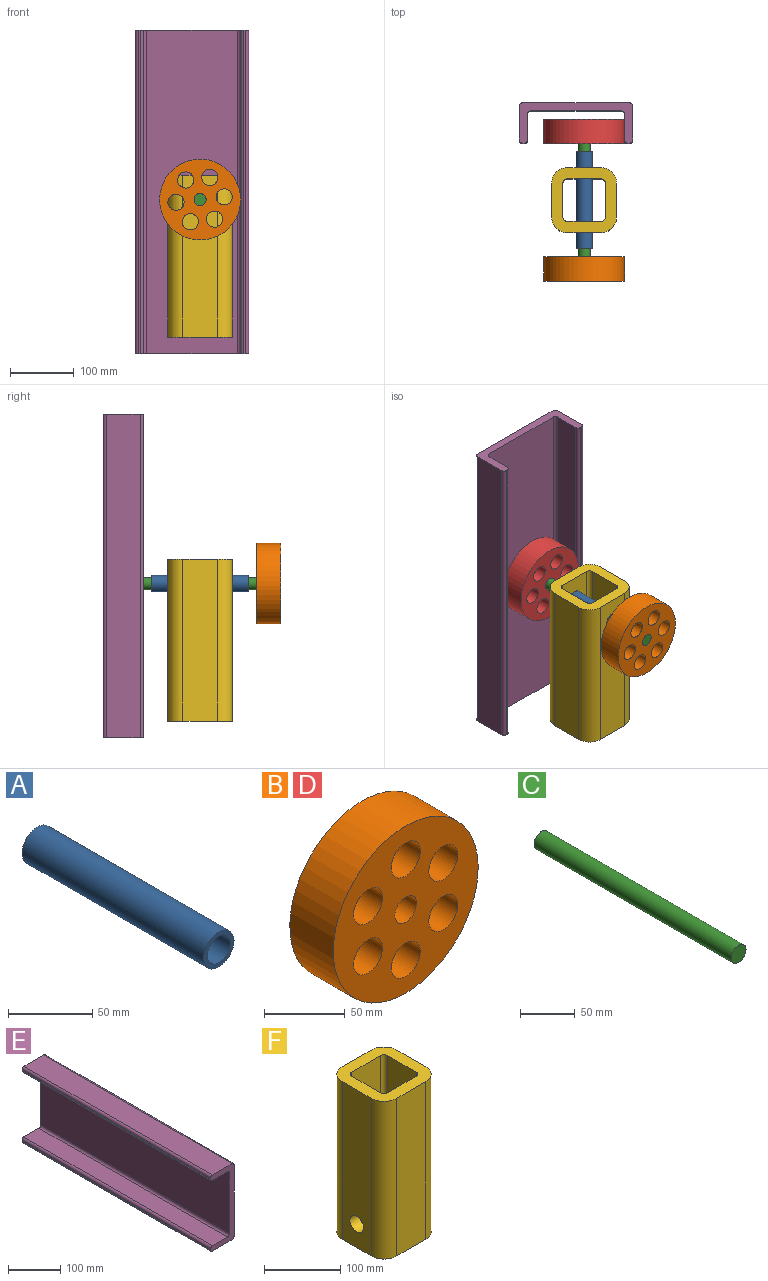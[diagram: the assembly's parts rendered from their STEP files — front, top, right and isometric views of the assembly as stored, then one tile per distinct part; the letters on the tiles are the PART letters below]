
ASSEMBLY  parts=6 mates=5
PART A: 4 faces, bbox 25.4x152.4x25.4 mm
  f0: cylinder r=9.53mm len=152.4mm, axis (0,1,0), area 9120.7mm2, adj f2,f3
  f1: cylinder r=12.7mm len=152.4mm, axis (0,1,0), area 12161mm2, adj f2,f3
  f2: plane 25.4x25.4mm, normal (0,-1,0), area 221.7mm2, adj f0,f1
  f3: plane 25.4x25.4mm, normal (0,1,0), area 221.7mm2, adj f0,f1
PART B: 10 faces, bbox 127x38.1x127 mm
  f0: cylinder r=9.53mm len=38.1mm, axis (0,1,0), area 2280.2mm2, adj f2,f3
  f1: cylinder r=63.5mm len=127mm, axis (0,1,0), area 15201.2mm2, adj f2,f3
  f2: plane 127x127mm, normal (0,-1,0), area 9342.4mm2, adj f0,f1,f4,f5,f6,f7,f8,f9
  f3: plane 127x127mm, normal (0,1,0), area 9342.4mm2, adj f0,f1,f4,f5,f6,f7,f8,f9
  f4: cylinder r=12.7mm len=38.1mm, axis (0,-1,0), area 3040.2mm2, adj f2,f3
  f5: cylinder r=12.7mm len=38.1mm, axis (0,-1,0), area 3040.2mm2, adj f2,f3
  f6: cylinder r=12.7mm len=38.1mm, axis (0,-1,0), area 3040.2mm2, adj f2,f3
  f7: cylinder r=12.7mm len=38.1mm, axis (0,-1,0), area 3040.2mm2, adj f2,f3
  f8: cylinder r=12.7mm len=38.1mm, axis (0,-1,0), area 3040.2mm2, adj f2,f3
  f9: cylinder r=12.7mm len=38.1mm, axis (0,-1,0), area 3040.2mm2, adj f2,f3
PART C: 3 faces, bbox 19.1x254x19.1 mm
  f0: cylinder r=9.53mm len=254mm, axis (0,1,0), area 15201.2mm2, adj f1,f2
  f1: plane 19.05x19.05mm, normal (0,-1,0), area 285mm2, adj f0
  f2: plane 19.05x19.05mm, normal (0,1,0), area 285mm2, adj f0
PART D: same geometry as B
PART E: 18 faces, bbox 63.5x508x177.8 mm
  f0: plane 508x167.64mm, normal (1,0,0), area 85161.1mm2, adj f8,f9,f10,f17
  f1: plane 508x53.34mm, normal (0,0,1), area 27096.7mm2, adj f8,f9,f10,f11
  f2: plane 508x2.54mm, normal (-1,0,0), area 1290.3mm2, adj f8,f9,f11,f12
  f3: plane 508x40.64mm, normal (0,0,-1), area 20645.1mm2, adj f8,f9,f12,f13
  f4: plane 508x142.24mm, normal (-1,0,0), area 72257.9mm2, adj f8,f9,f13,f14
  f5: plane 508x40.64mm, normal (0,0,1), area 20645.1mm2, adj f8,f9,f14,f15
  f6: plane 508x2.54mm, normal (-1,0,0), area 1290.3mm2, adj f8,f9,f15,f16
  f7: plane 508x53.34mm, normal (0,0,-1), area 27096.7mm2, adj f8,f9,f16,f17
  f8: plane 177.8x63.5mm, normal (0,-1,0), area 3526.2mm2, adj f0,f1,f2,f3,f4,f5,f6,f7
  f9: plane 177.8x63.5mm, normal (0,1,0), area 3526.2mm2, adj f0,f1,f2,f3,f4,f5,f6,f7
  f10: cylinder r=5.08mm len=508mm, axis (0,1,0), area 4053.7mm2, adj f0,f1,f8,f9
  f11: cylinder r=5.08mm len=508mm, axis (0,-1,0), area 4053.7mm2, adj f1,f2,f8,f9
  f12: cylinder r=5.08mm len=508mm, axis (0,1,0), area 4053.7mm2, adj f2,f3,f8,f9
  f13: cylinder r=5.08mm len=508mm, axis (0,-1,0), area 4053.7mm2, adj f3,f4,f8,f9
  f14: cylinder r=5.08mm len=508mm, axis (0,1,0), area 4053.7mm2, adj f4,f5,f8,f9
  f15: cylinder r=5.08mm len=508mm, axis (0,-1,0), area 4053.7mm2, adj f5,f6,f8,f9
  f16: cylinder r=5.08mm len=508mm, axis (0,1,0), area 4053.7mm2, adj f6,f7,f8,f9
  f17: cylinder r=5.08mm len=508mm, axis (0,-1,0), area 4053.7mm2, adj f0,f7,f8,f9
PART F: 20 faces, bbox 101.6x101.6x254 mm
  f0: plane 254x53.85mm, normal (0,-1,0), area 13677.4mm2, adj f1,f15,f16,f17
  f1: cylinder r=23.88mm len=254mm, axis (0,0,-1), area 9526.1mm2, adj f0,f2,f16,f17
  f2: plane 254x53.85mm, normal (1,0,0), area 13170.7mm2, adj f1,f3,f16,f17,f19
  f3: cylinder r=23.88mm len=254mm, axis (0,0,-1), area 9526.1mm2, adj f2,f4,f16,f17
  f4: plane 254x53.85mm, normal (0,1,0), area 13677.4mm2, adj f3,f5,f16,f17
  f5: cylinder r=23.88mm len=254mm, axis (0,0,-1), area 9526.1mm2, adj f4,f6,f16,f17
  f6: plane 254x53.85mm, normal (-1,0,0), area 13170.7mm2, adj f5,f15,f16,f17,f18
  f7: cylinder r=6.35mm len=254mm, axis (0,0,-1), area 2533.5mm2, adj f8,f14,f16,f17
  f8: plane 254x53.85mm, normal (-1,0,0), area 13170.7mm2, adj f7,f9,f16,f17,f19
  f9: cylinder r=6.35mm len=254mm, axis (0,0,-1), area 2533.5mm2, adj f8,f10,f16,f17
  f10: plane 254x53.85mm, normal (0,1,0), area 13677.4mm2, adj f9,f11,f16,f17
  f11: cylinder r=6.35mm len=254mm, axis (0,0,-1), area 2533.5mm2, adj f10,f12,f16,f17
  f12: plane 254x53.85mm, normal (1,0,0), area 13170.7mm2, adj f11,f13,f16,f17,f18
  f13: cylinder r=6.35mm len=254mm, axis (0,0,-1), area 2533.5mm2, adj f12,f14,f16,f17
  f14: plane 254x53.85mm, normal (0,-1,0), area 13677.4mm2, adj f7,f13,f16,f17
  f15: cylinder r=23.88mm len=254mm, axis (0,0,-1), area 9526.1mm2, adj f0,f6,f16,f17
  f16: plane 101.6x101.6mm, normal (0,0,1), area 5439.2mm2, adj f0,f1,f2,f3,f4,f5,f6,f7
  f17: plane 101.6x101.6mm, normal (0,0,-1), area 5439.2mm2, adj f0,f1,f2,f3,f4,f5,f6,f7
  f18: cylinder r=12.7mm len=25.4mm, axis (1,0,0), area 1398.5mm2, adj f6,f12
  f19: cylinder r=12.7mm len=25.4mm, axis (1,0,0), area 1398.5mm2, adj f2,f8
PLACE A t=(12.7,-76.2,-11.88)mm
PLACE B rot(axis=(0,1,0),23.7deg) t=(12.7,-241.3,-11.88)mm
PLACE C rot(axis=(0,1,0),23.7deg) t=(12.7,-25.4,-11.88)mm
PLACE D rot(axis=(0,1,0),23.7deg) t=(12.7,-25.4,-11.88)mm
PLACE E rot(axis=(-0.58,-0.58,0.58),120deg) t=(76.2,-12.7,-254)mm
PLACE F rot(axis=(0.71,0.71,0),180deg) t=(12.7,-152.4,26.22)mm
MATE fastened B.f0 <-> C.f0  axis (0,-1,0) through (12.7,-279.4,-11.88)mm
MATE fastened C.f0 <-> D.f0  axis (0,1,0) through (12.7,-25.4,-11.88)mm
MATE revolute C.f0 <-> A.f1  axis (0,1,0) through (12.7,-152.4,-11.88)mm
MATE slider F.f16 <-> E.f9  axis (0,0,-1) through (12.7,-101.6,-227.78)mm
MATE fastened A.f0 <-> F.f18  axis (0,-1,0) through (12.7,-228.6,-11.88)mm
